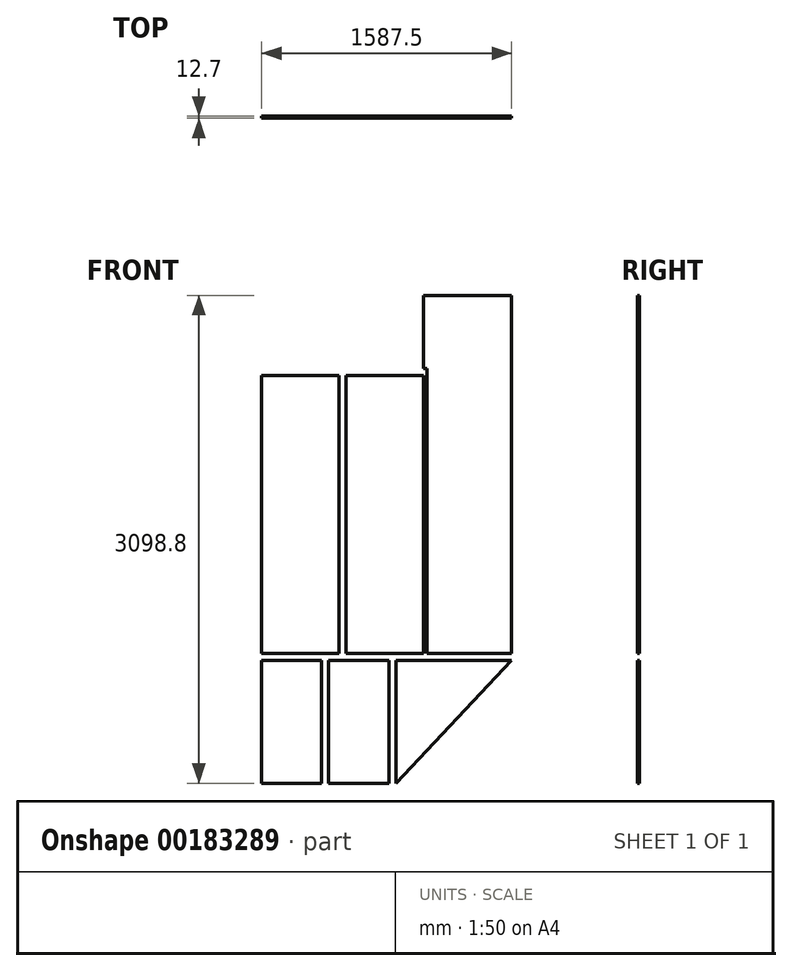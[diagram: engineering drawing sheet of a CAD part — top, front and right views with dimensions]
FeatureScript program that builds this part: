
annotation { "Feature Type Name" : "Feature", "Feature Type Description" : "" }
export const myFeature = defineFeature(function(context is Context, id is Id, definition is map)
    precondition{}
    {
        {
            var Q0;
            Q0=qCreatedBy(makeId("Front.planeOp"),FACE);
            var sketch = newSketch(context, id + "F0", { "sketchPlane" : qUnion([Q0])});
            skLineSegment(sketch, "E0", {"start": v(-1159.5, -2577.8) * mm, "end": v(-1159.5, 1524.3) * mm});
            skLineSegment(sketch, "E1", {"start": v(-1159.5, -2577.8) * mm, "end": v(-1070.6, -2577.8) * mm});
            skLineSegment(sketch, "E2", {"start": v(-1070.6, -2577.8) * mm, "end": v(-1070.6, -2730.2) * mm});
            skLineSegment(sketch, "E3", {"start": v(-1070.6, -2730.2) * mm, "end": v(-1311.9, -2730.2) * mm});
            skLineSegment(sketch, "E4", {"start": v(-1311.9, -2730.2) * mm, "end": v(-1311.9, 1676.7) * mm});
            skLineSegment(sketch, "E5", {"start": v(-1159.5, 1524.3) * mm, "end": v(-86.36, 1524.3) * mm});
            skLineSegment(sketch, "E6", {"start": v(-1311.9, 1676.7) * mm, "end": v(-238.76, 1676.7) * mm});
            skLineSegment(sketch, "E7", {"start": v(-86.36, 1524.3) * mm, "end": v(-86.36, 1987.85) * mm});
            skLineSegment(sketch, "E8", {"start": v(-238.76, 1676.7) * mm, "end": v(-238.76, 2140.25) * mm});
            skLineSegment(sketch, "E9", {"start": v(-86.36, 1987.85) * mm, "end": v(516.9, 1987.85) * mm});
            skLineSegment(sketch, "E10", {"start": v(-238.76, 2140.25) * mm, "end": v(364.5, 2140.25) * mm});
            skLineSegment(sketch, "E11", {"start": v(364.5, 2140.25) * mm, "end": v(364.5, 2165.65) * mm});
            skLineSegment(sketch, "E12", {"start": v(364.5, 2165.65) * mm, "end": v(1812.3, 2165.65) * mm});
            skLineSegment(sketch, "E13", {"start": v(516.9, 1987.85) * mm, "end": v(516.9, 2140.25) * mm});
            skLineSegment(sketch, "E14", {"start": v(516.9, 2140.25) * mm, "end": v(1609.1, 2140.25) * mm});
            skLineSegment(sketch, "E15", {"start": v(1812.3, 2165.65) * mm, "end": v(1812.3, 2140.25) * mm});
            skLineSegment(sketch, "E16", {"start": v(1609.1, 2140.25) * mm, "end": v(1609.1, 1987.85) * mm});
            skLineSegment(sketch, "E17", {"start": v(1609.1, 1987.85) * mm, "end": v(1710.7, 1987.85) * mm});
            skLineSegment(sketch, "E18", {"start": v(1812.3, 2140.25) * mm, "end": v(1863.1, 2140.25) * mm});
            skLineSegment(sketch, "E19", {"start": v(1710.7, 1987.85) * mm, "end": v(1710.7, -1853.9) * mm});
            skLineSegment(sketch, "E20", {"start": v(1710.7, -1853.9) * mm, "end": v(974.1, -1853.9) * mm});
            skLineSegment(sketch, "E21", {"start": v(974.1, -1853.9) * mm, "end": v(974.1, -2006.3) * mm});
            skLineSegment(sketch, "E22", {"start": v(974.1, -2006.3) * mm, "end": v(1317, -2006.3) * mm});
            skLineSegment(sketch, "E23", {"start": v(-1070.6, -2577.8) * mm, "end": v(-187.96, -2577.8) * mm});
            skLineSegment(sketch, "E24", {"start": v(-1070.6, -2730.2) * mm, "end": v(-187.96, -2730.2) * mm});
            skLineSegment(sketch, "E25", {"start": v(-187.96, -2730.2) * mm, "end": v(-187.96, -2577.8) * mm});
            skLineSegment(sketch, "E26", {"start": v(-187.96, -2577.8) * mm, "end": v(-124.46, -2577.8) * mm});
            skLineSegment(sketch, "E27", {"start": v(1317, -2006.3) * mm, "end": v(1317, -2577.8) * mm});
            skLineSegment(sketch, "E28", {"start": v(1317, -2577.8) * mm, "end": v(27.94, -2577.8) * mm});
            skLineSegment(sketch, "E29", {"start": v(-124.46, -2577.8) * mm, "end": v(-124.46, -1853.9) * mm});
            skLineSegment(sketch, "E30", {"start": v(-124.46, -1853.9) * mm, "end": v(180.34, -1853.9) * mm});
            skLineSegment(sketch, "E31", {"start": v(27.94, -2577.8) * mm, "end": v(27.94, -2006.3) * mm});
            skLineSegment(sketch, "E32", {"start": v(974.1, -1853.9) * mm, "end": v(218.44, -1853.9) * mm});
            skLineSegment(sketch, "E33", {"start": v(974.1, -2006.3) * mm, "end": v(218.44, -2006.3) * mm});
            skLineSegment(sketch, "E34", {"start": v(218.44, -1853.9) * mm, "end": v(218.44, -2006.3) * mm});
            skLineSegment(sketch, "E35", {"start": v(27.94, -2006.3) * mm, "end": v(180.34, -2006.3) * mm});
            skLineSegment(sketch, "E36", {"start": v(180.34, -1853.9) * mm, "end": v(180.34, -2006.3) * mm});
            skLineSegment(sketch, "E37", {"start": v(-187.96, -2730.2) * mm, "end": v(1469.4, -2730.2) * mm});
            skLineSegment(sketch, "E38", {"start": v(1469.4, -2730.2) * mm, "end": v(1469.4, -2006.3) * mm});
            skLineSegment(sketch, "E39", {"start": v(1469.4, -2006.3) * mm, "end": v(1863.1, -2006.3) * mm});
            skLineSegment(sketch, "E40", {"start": v(1863.1, -2006.3) * mm, "end": v(1863.1, 2140.25) * mm});
            skLineSegment(sketch, "E41", {"start": v(180.34, -2006.3) * mm, "end": v(218.44, -2006.3) * mm});
            skLineSegment(sketch, "E42", {"start": v(180.34, -1853.9) * mm, "end": v(218.44, -1853.9) * mm});
            skLineSegment(sketch, "E43", {"start": v(516.9, 1987.85) * mm, "end": v(1609.1, 1987.85) * mm});
            skLineSegment(sketch, "E44.top", {"start": v(-1159.5, 1479.85) * mm, "end": v(-86.36, 1479.85) * mm});
            skLineSegment(sketch, "E44.left", {"start": v(-1159.5, 1524.3) * mm, "end": v(-1159.5, 1479.85) * mm});
            skLineSegment(sketch, "E44.right", {"start": v(472.44, 1524.3) * mm, "end": v(472.44, 1479.85) * mm});
            skLineSegment(sketch, "E45.bottom", {"start": v(-1159.5, 1479.85) * mm, "end": v(-1115.06, 1479.85) * mm});
            skLineSegment(sketch, "E45.top", {"start": v(-1159.5, -1110.95) * mm, "end": v(-1115.06, -1110.95) * mm});
            skLineSegment(sketch, "E45.left", {"start": v(-1159.5, 1479.85) * mm, "end": v(-1159.5, -1110.95) * mm});
            skLineSegment(sketch, "E45.right", {"start": v(-1115.06, 1479.85) * mm, "end": v(-1115.06, -1110.95) * mm});
            skLineSegment(sketch, "E46.bottom", {"start": v(-86.36, 1987.85) * mm, "end": v(-41.9, 1987.85) * mm});
            skLineSegment(sketch, "E46.left", {"start": v(-86.36, 1987.85) * mm, "end": v(-86.36, 1524.3) * mm});
            skLineSegment(sketch, "E46.right", {"start": v(-41.9, 1987.85) * mm, "end": v(-41.9, 1524.3) * mm});
            skLineSegment(sketch, "E47.bottom", {"start": v(516.9, 1987.85) * mm, "end": v(472.44, 1987.85) * mm});
            skLineSegment(sketch, "E47.left", {"start": v(516.9, 1987.85) * mm, "end": v(516.9, -348.95) * mm});
            skLineSegment(sketch, "E47.right", {"start": v(472.44, 1987.85) * mm, "end": v(472.44, -330.53) * mm});
            skLineSegment(sketch, "E48.bottom", {"start": v(-1159.5, -1110.95) * mm, "end": v(-263.52, -1110.95) * mm});
            skLineSegment(sketch, "E48.top", {"start": v(-1159.5, -1155.4) * mm, "end": v(-245.1, -1155.4) * mm});
            skLineSegment(sketch, "E48.left", {"start": v(-1159.5, -1110.95) * mm, "end": v(-1159.5, -1155.4) * mm});
            skLineSegment(sketch, "E49", {"start": v(-245.1, -1155.4) * mm, "end": v(-263.52, -1110.95) * mm});
            skLineSegment(sketch, "E50", {"start": v(516.9, -348.95) * mm, "end": v(472.44, -330.53) * mm});
            skLineSegment(sketch, "E51", {"start": v(-245.1, -1155.4) * mm, "end": v(516.9, -348.95) * mm});
            skLineSegment(sketch, "E52", {"start": v(-263.52, -1110.95) * mm, "end": v(472.44, -330.53) * mm});
            skLineSegment(sketch, "E53.bottom", {"start": v(-41.9, 1987.85) * mm, "end": v(472.44, 1987.85) * mm});
            skLineSegment(sketch, "E53.top", {"start": v(-41.9, 1943.4) * mm, "end": v(472.44, 1943.4) * mm});
            skLineSegment(sketch, "E53.left", {"start": v(-41.9, 1987.85) * mm, "end": v(-41.9, 1943.4) * mm});
            skLineSegment(sketch, "E53.right", {"start": v(472.44, 1987.85) * mm, "end": v(472.44, 1943.4) * mm});
            skLineSegment(sketch, "E54.bottom", {"start": v(472.44, -330.53) * mm, "end": v(-1115.06, -330.53) * mm});
            skLineSegment(sketch, "E54.top", {"start": v(472.44, -286.08) * mm, "end": v(-1115.06, -286.08) * mm});
            skLineSegment(sketch, "E54.left", {"start": v(472.44, -330.53) * mm, "end": v(472.44, -286.08) * mm});
            skLineSegment(sketch, "E54.right", {"start": v(-1115.06, -330.53) * mm, "end": v(-1115.06, -286.08) * mm});
            skLineSegment(sketch, "E55.bottom", {"start": v(-263.52, -1110.95) * mm, "end": v(-307.97, -1110.95) * mm});
            skLineSegment(sketch, "E55.top", {"start": v(-263.52, -330.53) * mm, "end": v(-307.97, -330.53) * mm});
            skLineSegment(sketch, "E55.left", {"start": v(-263.52, -1110.95) * mm, "end": v(-263.52, -330.53) * mm});
            skLineSegment(sketch, "E55.right", {"start": v(-307.97, -1110.95) * mm, "end": v(-307.97, -330.53) * mm});
            skLineSegment(sketch, "E56.top", {"start": v(-86.36, -286.08) * mm, "end": v(-41.9, -286.08) * mm});
            skLineSegment(sketch, "E56.left", {"start": v(-86.36, 1524.3) * mm, "end": v(-86.36, -286.08) * mm});
            skLineSegment(sketch, "E56.right", {"start": v(-41.9, 1524.3) * mm, "end": v(-41.9, -286.08) * mm});
            skLineSegment(sketch, "E57.trimOffspring", {"start": v(-41.9, 1479.85) * mm, "end": v(472.44, 1479.85) * mm});
            skLineSegment(sketch, "E58.trimOffspring", {"start": v(-41.9, 1524.3) * mm, "end": v(472.44, 1524.3) * mm});
            skLineSegment(sketch, "E59.bottom", {"start": v(-622.93, 1479.85) * mm, "end": v(-578.48, 1479.85) * mm});
            skLineSegment(sketch, "E59.top", {"start": v(-622.93, -286.08) * mm, "end": v(-578.48, -286.08) * mm});
            skLineSegment(sketch, "E59.left", {"start": v(-622.93, 1479.85) * mm, "end": v(-622.93, -286.08) * mm});
            skLineSegment(sketch, "E59.right", {"start": v(-578.48, 1479.85) * mm, "end": v(-578.48, -286.08) * mm});
            skLineSegment(sketch, "E60.bottom", {"start": v(-734.06, -330.53) * mm, "end": v(-689.6, -330.53) * mm});
            skLineSegment(sketch, "E60.top", {"start": v(-734.06, -1110.95) * mm, "end": v(-689.6, -1110.95) * mm});
            skLineSegment(sketch, "E60.left", {"start": v(-734.06, -330.53) * mm, "end": v(-734.06, -1110.95) * mm});
            skLineSegment(sketch, "E60.right", {"start": v(-689.6, -330.53) * mm, "end": v(-689.6, -1110.95) * mm});
            skLineSegment(sketch, "E61.bottom", {"start": v(472.44, 1073.45) * mm, "end": v(-41.9, 1073.45) * mm});
            skLineSegment(sketch, "E61.top", {"start": v(472.44, 1029) * mm, "end": v(-41.9, 1029) * mm});
            skLineSegment(sketch, "E61.left", {"start": v(472.44, 1073.45) * mm, "end": v(472.44, 1029) * mm});
            skLineSegment(sketch, "E61.right", {"start": v(-41.9, 1073.45) * mm, "end": v(-41.9, 1029) * mm});
            skLineSegment(sketch, "E62.bottom", {"start": v(-41.9, 399.97) * mm, "end": v(472.44, 399.97) * mm});
            skLineSegment(sketch, "E62.top", {"start": v(-41.9, 355.52) * mm, "end": v(472.44, 355.52) * mm});
            skLineSegment(sketch, "E62.left", {"start": v(-41.9, 399.97) * mm, "end": v(-41.9, 355.52) * mm});
            skLineSegment(sketch, "E62.right", {"start": v(472.44, 399.97) * mm, "end": v(472.44, 355.52) * mm});
            skLineSegment(sketch, "E63.bottom", {"start": v(-578.48, 625.4) * mm, "end": v(-86.36, 625.4) * mm});
            skLineSegment(sketch, "E63.top", {"start": v(-578.48, 580.95) * mm, "end": v(-86.36, 580.95) * mm});
            skLineSegment(sketch, "E63.left", {"start": v(-578.48, 625.4) * mm, "end": v(-578.48, 580.95) * mm});
            skLineSegment(sketch, "E63.right", {"start": v(-86.36, 625.4) * mm, "end": v(-86.36, 580.95) * mm});
            skLineSegment(sketch, "E64.bottom", {"start": v(-622.93, 625.4) * mm, "end": v(-1115.06, 625.4) * mm});
            skLineSegment(sketch, "E64.top", {"start": v(-622.93, 580.95) * mm, "end": v(-1115.06, 580.95) * mm});
            skLineSegment(sketch, "E64.left", {"start": v(-622.93, 625.4) * mm, "end": v(-622.93, 580.95) * mm});
            skLineSegment(sketch, "E64.right", {"start": v(-1115.06, 625.4) * mm, "end": v(-1115.06, 580.95) * mm});
            skLineSegment(sketch, "E65.bottom", {"start": v(-1159.5, 1524.3) * mm, "end": v(-64.13, 1524.3) * mm});
            skLineSegment(sketch, "E65.top", {"start": v(-1159.5, -308.3) * mm, "end": v(-64.13, -308.3) * mm});
            skLineSegment(sketch, "E65.left", {"start": v(-1159.5, 1524.3) * mm, "end": v(-1159.5, -308.3) * mm});
            skLineSegment(sketch, "E65.right", {"start": v(-64.13, 1524.3) * mm, "end": v(-64.13, -308.3) * mm});
            skLineSegment(sketch, "E66.bottom", {"start": v(-64.13, -308.3) * mm, "end": v(472.44, -308.3) * mm});
            skLineSegment(sketch, "E66.top", {"start": v(-64.13, 1987.85) * mm, "end": v(472.44, 1987.85) * mm});
            skLineSegment(sketch, "E66.left", {"start": v(-64.13, -308.3) * mm, "end": v(-64.13, -286.08) * mm});
            skLineSegment(sketch, "E66.right", {"start": v(472.44, -308.3) * mm, "end": v(472.44, 1987.85) * mm});
            skLineSegment(sketch, "E67.bottom", {"start": v(-64.13, 1987.85) * mm, "end": v(-86.36, 1987.85) * mm});
            skLineSegment(sketch, "E67.top", {"start": v(-64.13, 1524.3) * mm, "end": v(-86.36, 1524.3) * mm});
            skLineSegment(sketch, "E68.bottom", {"start": v(-1159.5, -308.3) * mm, "end": v(472.44, -308.3) * mm});
            skLineSegment(sketch, "E68.left", {"start": v(-1159.5, -308.3) * mm, "end": v(-1159.5, -1110.95) * mm});
            skLineSegment(sketch, "E68.right", {"start": v(472.44, -308.3) * mm, "end": v(472.44, -330.53) * mm});
            skSolve(sketch);
        }
        {
            var Q0;
            {var subQ3=sQuery(id+"F0.wireOp",EDGE,"E68.left");Q0=makeQuery(id+"F0.imprint","IMPRINT",FACE,{"disambiguationData":[TD([[makeQuery(id+"F0.imprint","IMPRINT",EDGE,{"derivedFrom":subQ3}),1.0]])]});}
            var Q1;
            {var subQ5=sQuery(id+"F0.wireOp",EDGE,"E60.left");Q1=makeQuery(id+"F0.imprint","IMPRINT",FACE,{"disambiguationData":[TD([[makeQuery(id+"F0.imprint","IMPRINT",EDGE,{"derivedFrom":subQ5}),-1.0]])]});}
            var Q2;
            {var subQ6=sQuery(id+"F0.wireOp",EDGE,"E55.top");Q2=makeQuery(id+"F0.imprint","IMPRINT",FACE,{"disambiguationData":[TD([[makeQuery(id+"F0.imprint","IMPRINT",EDGE,{"derivedFrom":subQ6}),-1.0]])]});}
            var Q3;
            Q3=makeQuery(id+"F0.imprint","IMPRINT",FACE,{"disambiguationData":[TD([[makeQuery(id+"F0.imprint","IMPRINT",EDGE,{"derivedFrom":sQuery(id+"F0.wireOp",EDGE,"E60.bottom")}),-1.0]])]});
            var Q4;
            Q4=makeQuery(id+"F0.imprint","IMPRINT",FACE,{"disambiguationData":[TD([[makeQuery(id+"F0.imprint","IMPRINT",EDGE,{"derivedFrom":sQuery(id+"F0.wireOp",EDGE,"E55.top")}),1.0]])]});
            var Q5;
            {var subQ0=sQuery(id+"F0.wireOp",EDGE,"E55.right");Q5=makeQuery(id+"F0.imprint","IMPRINT",FACE,{"disambiguationData":[TD([[makeQuery(id+"F0.imprint","IMPRINT",EDGE,{"derivedFrom":subQ0}),1.0]])]});}
            var Q6;
            {var subQ0=sQuery(id+"F0.wireOp",EDGE,"E52");Q6=makeQuery(id+"F0.imprint","IMPRINT",FACE,{"disambiguationData":[TD([[makeQuery(id+"F0.imprint","IMPRINT",EDGE,{"derivedFrom":subQ0}),1.0]])]});}
            extrude(context, id + "F1", {"entities" : qUnion([Q0, Q1, Q2, Q3, Q4, Q5, Q6]), "depth" : 12.7 * mm});
        }
        {
            var Q0;
            {var subQ3=sQuery(id+"F0.wireOp",EDGE,"E64.top");Q0=makeQuery(id+"F0.imprint","IMPRINT",FACE,{"disambiguationData":[TD([[makeQuery(id+"F0.imprint","IMPRINT",EDGE,{"derivedFrom":subQ3}),1.0]])]});}
            var Q1;
            {var subQ5=sQuery(id+"F0.wireOp",EDGE,"E63.top");Q1=makeQuery(id+"F0.imprint","IMPRINT",FACE,{"disambiguationData":[TD([[makeQuery(id+"F0.imprint","IMPRINT",EDGE,{"derivedFrom":subQ5}),-1.0]])]});}
            var Q2;
            {var subQ4=sQuery(id+"F0.wireOp",EDGE,"E59.bottom");Q2=makeQuery(id+"F0.imprint","IMPRINT",FACE,{"disambiguationData":[TD([[makeQuery(id+"F0.imprint","IMPRINT",EDGE,{"derivedFrom":subQ4}),-1.0]])]});}
            var Q3;
            {var subQ4=sQuery(id+"F0.wireOp",EDGE,"E59.top");Q3=makeQuery(id+"F0.imprint","IMPRINT",FACE,{"disambiguationData":[TD([[makeQuery(id+"F0.imprint","IMPRINT",EDGE,{"derivedFrom":subQ4}),-1.0]])]});}
            var Q4;
            {var subQ3=sQuery(id+"F0.wireOp",EDGE,"E63.right");Q4=makeQuery(id+"F0.imprint","IMPRINT",FACE,{"disambiguationData":[TD([[makeQuery(id+"F0.imprint","IMPRINT",EDGE,{"derivedFrom":subQ3}),1.0]])]});}
            var Q5;
            Q5=makeQuery(id+"F0.imprint","IMPRINT",FACE,{"disambiguationData":[TD([[makeQuery(id+"F0.imprint","IMPRINT",EDGE,{"derivedFrom":sQuery(id+"F0.wireOp",EDGE,"E63.bottom")}),-1.0]])]});
            var Q6;
            Q6=makeQuery(id+"F0.imprint","IMPRINT",FACE,{"disambiguationData":[TD([[makeQuery(id+"F0.imprint","IMPRINT",EDGE,{"derivedFrom":sQuery(id+"F0.wireOp",EDGE,"E64.bottom")}),1.0]])]});
            var Q7;
            {var subQ5=sQuery(id+"F0.wireOp",EDGE,"E64.bottom");Q7=makeQuery(id+"F0.imprint","IMPRINT",FACE,{"disambiguationData":[TD([[makeQuery(id+"F0.imprint","IMPRINT",EDGE,{"derivedFrom":subQ5}),-1.0]])]});}
            var Q8;
            {var subQ5=sQuery(id+"F0.wireOp",EDGE,"E63.bottom");Q8=makeQuery(id+"F0.imprint","IMPRINT",FACE,{"disambiguationData":[TD([[makeQuery(id+"F0.imprint","IMPRINT",EDGE,{"derivedFrom":subQ5}),1.0]])]});}
            var Q9;
            {var subQ5=sQuery(id+"F0.wireOp",EDGE,"E45.bottom");Q9=makeQuery(id+"F0.imprint","IMPRINT",FACE,{"disambiguationData":[TD([[makeQuery(id+"F0.imprint","IMPRINT",EDGE,{"derivedFrom":subQ5}),1.0]])]});}
            var Q10;
            {var subQ6=sQuery(id+"F0.wireOp",EDGE,"E45.bottom");Q10=makeQuery(id+"F0.imprint","IMPRINT",FACE,{"disambiguationData":[TD([[makeQuery(id+"F0.imprint","IMPRINT",EDGE,{"derivedFrom":subQ6}),-1.0]])]});}
            extrude(context, id + "F2", {"entities" : qUnion([Q0, Q1, Q2, Q3, Q4, Q5, Q6, Q7, Q8, Q9, Q10]), "operationType" : NewBodyOperationType.ADD, "depth" : 12.7 * mm});
        }
        {
            var Q0;
            {var subQ5=sQuery(id+"F0.wireOp",EDGE,"E62.top");Q0=makeQuery(id+"F0.imprint","IMPRINT",FACE,{"disambiguationData":[TD([[makeQuery(id+"F0.imprint","IMPRINT",EDGE,{"derivedFrom":subQ5}),-1.0]])]});}
            var Q1;
            {var subQ0=sQuery(id+"F0.wireOp",EDGE,"E62.bottom");Q1=makeQuery(id+"F0.imprint","IMPRINT",FACE,{"disambiguationData":[TD([[makeQuery(id+"F0.imprint","IMPRINT",EDGE,{"derivedFrom":subQ0}),-1.0]])]});}
            var Q2;
            {var subQ0=sQuery(id+"F0.wireOp",EDGE,"E61.top");Q2=makeQuery(id+"F0.imprint","IMPRINT",FACE,{"disambiguationData":[TD([[makeQuery(id+"F0.imprint","IMPRINT",EDGE,{"derivedFrom":subQ0}),1.0]])]});}
            var Q3;
            {var subQ0=sQuery(id+"F0.wireOp",EDGE,"E57.trimOffspring");Q3=makeQuery(id+"F0.imprint","IMPRINT",FACE,{"disambiguationData":[TD([[makeQuery(id+"F0.imprint","IMPRINT",EDGE,{"derivedFrom":subQ0}),-1.0]])]});}
            var Q4;
            {var subQ0=sQuery(id+"F0.wireOp",EDGE,"E61.bottom");Q4=makeQuery(id+"F0.imprint","IMPRINT",FACE,{"disambiguationData":[TD([[makeQuery(id+"F0.imprint","IMPRINT",EDGE,{"derivedFrom":subQ0}),1.0]])]});}
            var Q5;
            {var subQ7=sQuery(id+"F0.wireOp",EDGE,"E46.right");Q5=makeQuery(id+"F0.imprint","IMPRINT",FACE,{"disambiguationData":[TD([[makeQuery(id+"F0.imprint","IMPRINT",EDGE,{"derivedFrom":subQ7}),-1.0]])]});}
            var Q6;
            {var subQ7=sQuery(id+"F0.wireOp",EDGE,"E66.left");Q6=makeQuery(id+"F0.imprint","IMPRINT",FACE,{"disambiguationData":[TD([[makeQuery(id+"F0.imprint","IMPRINT",EDGE,{"derivedFrom":subQ7}),-1.0]])]});}
            var Q7;
            {var subQ2=sQuery(id+"F0.wireOp",EDGE,"E57.trimOffspring");Q7=makeQuery(id+"F0.imprint","IMPRINT",FACE,{"disambiguationData":[TD([[makeQuery(id+"F0.imprint","IMPRINT",EDGE,{"derivedFrom":subQ2}),1.0]])]});}
            var Q8;
            {var subQ0=sQuery(id+"F0.wireOp",EDGE,"E53.top");Q8=makeQuery(id+"F0.imprint","IMPRINT",FACE,{"disambiguationData":[TD([[makeQuery(id+"F0.imprint","IMPRINT",EDGE,{"derivedFrom":subQ0}),1.0]])]});}
            var Q9;
            Q9=makeQuery(id+"F0.imprint","IMPRINT",FACE,{"disambiguationData":[TD([[makeQuery(id+"F0.imprint","IMPRINT",EDGE,{"derivedFrom":sQuery(id+"F0.wireOp",EDGE,"E46.right")}),1.0]])]});
            extrude(context, id + "F3", {"entities" : qUnion([Q0, Q1, Q2, Q3, Q4, Q5, Q6, Q7, Q8, Q9]), "operationType" : NewBodyOperationType.ADD, "depth" : 12.7 * mm});
        }
    });
